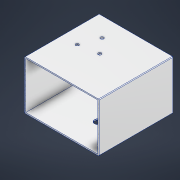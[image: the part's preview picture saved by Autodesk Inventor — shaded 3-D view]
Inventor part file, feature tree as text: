
AUTODESK INVENTOR PART (.ipt)
format: ipt  version: 2021 (Build 250183000, 183)  size: 278,528 bytes
history: native  units: mm
features: sketch x12, extrude x8, hole x4, chamfer x4, fillet x2, projected_geometry x1
ambient origin geometry x8: Origin, YZ Plane, XZ Plane, XY Plane, X Axis, Y Axis, Z Axis, Center Point
bodies: Solid1 (feature_tree)
feature tree (31):
  extrude  "base"  Depth=228.0mm
  hole  "centreHole"  [1 undecoded]
  chamfer  "holeChamfer"  Distance=115.0mm
  extrude  "walls"  Depth=111.5mm
  extrude  "platform"  Depth=228.0mm
  hole  "motorScrewHoles"  [1 undecoded]
  extrude  "motorShaftHole"  Depth=90.0mm TaperAngle=0.0deg
  chamfer  "Chamfer2"  Distance=80.0mm
  extrude  "Extrusion8"  Depth=4.0mm TaperAngle=45.0deg
  hole  "Hole4"  [1 undecoded]
  fillet  "Fillet2"  Radius=222.0mm
  extrude  "Extrusion9"  Depth=3.0mm
  fillet  "Fillet3"  Radius=65.0mm
  extrude  "Extrusion10"  Depth=20.0mm
  chamfer  "Chamfer3"  Distance=54.0mm
  extrude  "Extrusion11"  Depth=4.0mm
  chamfer  "Chamfer4"  Angle=120.0deg  [1 undecoded]
  hole  "Hole5"  [1 undecoded]
  sketch  "Sketch1"  dims[d0=3.0mm d1=0.0mm]
  sketch  "Sketch5"  dims[d19=17.0mm d20=8.0mm d21=4.0mm d22=2.0mm d23=90.0deg d24=8.0mm d25=20.594885mm d26=228.0mm]
  sketch  "Sketch7"  dims[d27=183.0mm d29=3.0mm d30=115.0mm d31=0.0mm]
  projected_geometry  "Projected Loop2"
  sketch  "Sketch10"  dims[d46=114.0mm d47=111.5mm]
  sketch  "Sketch11"  dims[d48=183.0mm d49=228.0mm]
  sketch  "Sketch12"  dims[d57=0.5mm d58=2.0mm d59=45.0deg d60=6.0mm]
  sketch  "Sketch13"  dims[d61=48.0mm d66=90.0mm d67=0.0mm]
  sketch  "Sketch14"  dims[d68=36.0mm d69=120.0deg d70=120.0deg d72=36.0mm d73=28.0mm]
  sketch  "Sketch15"  dims[d74=48.0mm]
  sketch  "Sketch16"  dims[d75=6.0mm d76=8.0mm d77=4.0mm d78=2.0mm d79=90.0deg d80=8.0mm d81=20.594885mm]
  sketch  "Sketch17"  dims[d82=28.0mm]
  sketch  "Sketch18"  dims[d83=25.0mm d84=80.0mm d85=0.0mm d86=0.5mm d87=2.0mm d88=45.0deg d91=139.0mm d92=222.0mm d93=3.0mm d94=65.0mm d95=20.0mm d96=54.0mm d97=0.0mm d98=36.0mm d99=120.0deg d100=120.0deg d101=36.0mm d103=6.0mm d104=8.0mm d105=4.0mm d106=2.0mm d107=90.0deg d108=8.0mm d109=20.594885mm d110=1.0mm d111=25.0mm d112=50.0mm d113=0.0mm d114=27.0mm d115=36.0mm d116=27.0mm d117=30.0mm d118=48.0mm d119=20.0mm d121=25.0mm d122=50.0mm d123=0.0mm d124=0.5mm d125=2.0mm d126=45.0deg d127=5.0mm d128=3.0mm d129=0.0mm d130=1.5mm d131=2.0mm d132=45.0deg d133=55.0mm d134=183.0mm d135=61.0mm d136=228.0mm d137=76.0mm d138=120.0deg d140=8.0mm d141=6.0mm d142=4.0mm d143=2.0mm d144=90.0deg d145=8.0mm d146=20.594885mm d147=120.0deg d149=13.962634mm]
note: 5 required parameter values undecoded (feature->parameter linkage not recoverable at this tier; creation-order binding heuristic only, values carry confidence <= 0.55)
